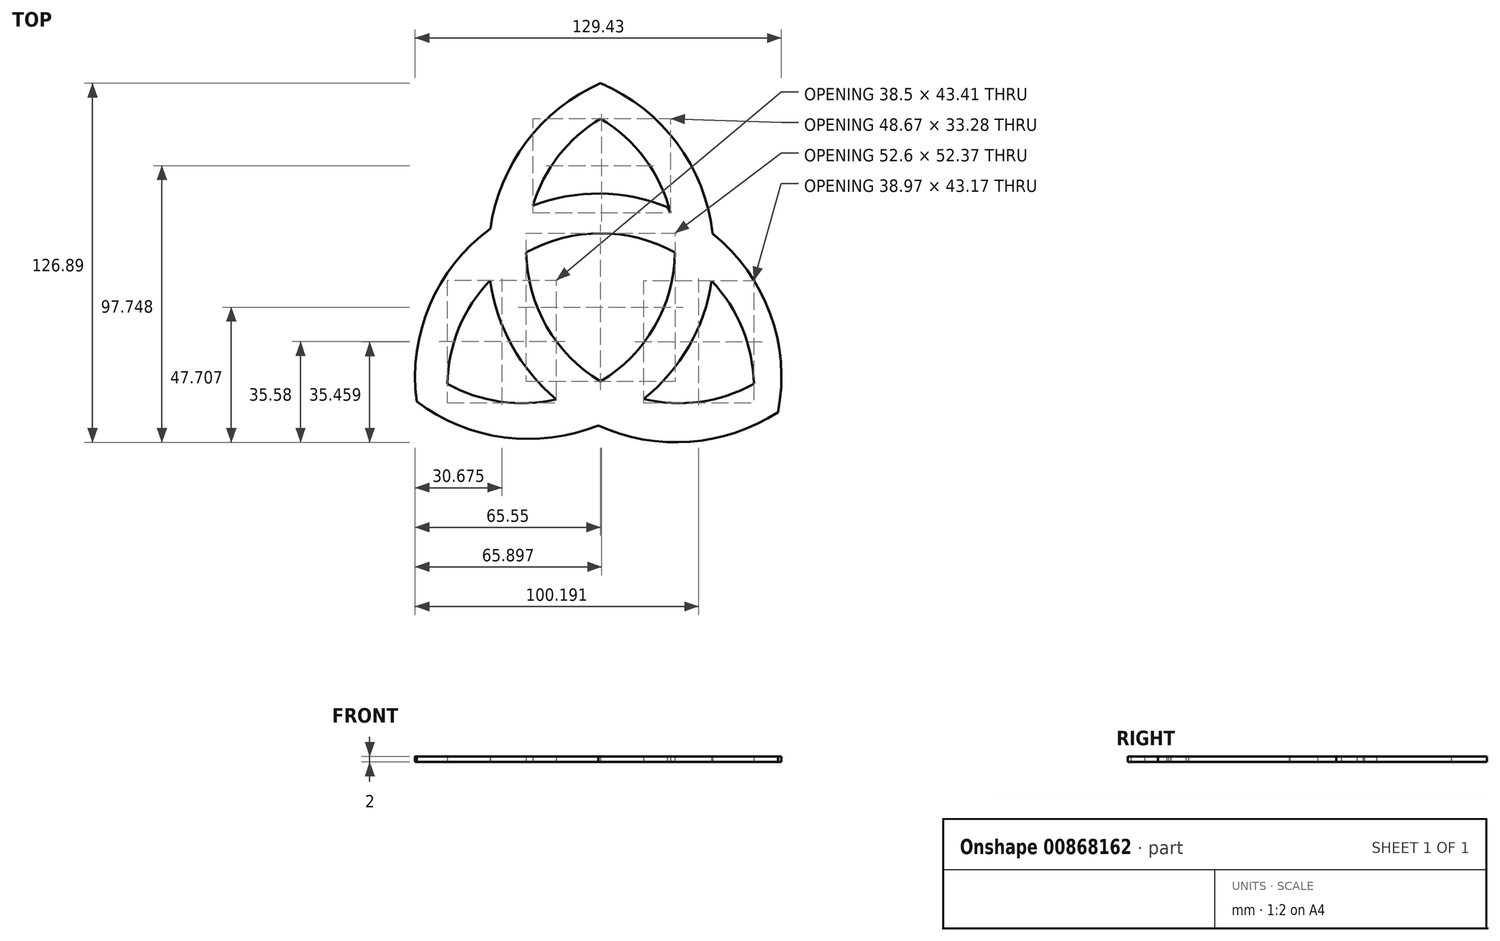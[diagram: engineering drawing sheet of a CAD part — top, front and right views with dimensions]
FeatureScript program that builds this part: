
annotation { "Feature Type Name" : "Feature", "Feature Type Description" : "" }
export const myFeature = defineFeature(function(context is Context, id is Id, definition is map)
    precondition{}
    {
        {
            var Q0;
            Q0=qCreatedBy(makeId("Top.planeOp"),FACE);
            var sketch = newSketch(context, id + "F0", { "sketchPlane" : qUnion([Q0])});
            skCircle(sketch, "E0", {"center": v(0, 0) * mm, "radius": 75 * mm});
            skCircle(sketch, "E1.cCircle", {"center": v(0, 0) * mm, "radius": 75 * mm, "construction": true});
            skLineSegment(sketch, "E1.0", {"start": v(23.6, 31.22) * mm, "end": v(24.68, 29.22) * mm});
            skLineSegment(sketch, "E2.0", {"start": v(25.24, 15.75) * mm, "end": v(26.26, 13.87) * mm});
            skArc(sketch, "E3", {"start": v(62.66, -41.22) * mm, "mid": v(59.93, -6.45) * mm, "end": v(39.56, 21.86) * mm});
            skArc(sketch, "E4", {"start": v(0, 75) * mm, "mid": v(-26.17, 54.36) * mm, "end": v(-38.97, 23.58) * mm});
            skArc(sketch, "E5", {"start": v(-64.95, -37.5) * mm, "mid": v(-34.02, -50.17) * mm, "end": v(-0.87, -45.91) * mm});
            skArc(sketch, "E6", {"start": v(54.13, -31.25) * mm, "mid": v(50.1, -11.65) * mm, "end": v(39.24, 5.16) * mm});
            skArc(sketch, "E7", {"start": v(0, 62.5) * mm, "mid": v(-14.86, 49.35) * mm, "end": v(-24, 31.73) * mm});
            skArc(sketch, "E8", {"start": v(-54.13, -31.25) * mm, "mid": v(-35.38, -37.54) * mm, "end": v(-15.62, -36.67) * mm});
            skArc(sketch, "E9.trimOffspring", {"start": v(-26.3, 15.18) * mm, "mid": v(0.76, -30.81) * mm, "end": v(54.13, -31.25) * mm});
            skArc(sketch, "E10.trimOffspring", {"start": v(-39.01, 5.4) * mm, "mid": v(-1, -45.86) * mm, "end": v(62.66, -41.22) * mm});
            skArc(sketch, "E11.trimOffspring", {"start": v(24.21, 30.97) * mm, "mid": v(-40.25, 22.63) * mm, "end": v(-64.95, -37.5) * mm});
            skArc(sketch, "E12.trimOffspring", {"start": v(26.3, 15.18) * mm, "mid": v(-27.07, 14.75) * mm, "end": v(-54.13, -31.25) * mm});
            skArc(sketch, "E13.trimOffspring", {"start": v(0, -30.37) * mm, "mid": v(26.3, 16.07) * mm, "end": v(0, 62.5) * mm});
            skArc(sketch, "E14.trimOffspring", {"start": v(15.16, -36.56) * mm, "mid": v(39.35, 23.53) * mm, "end": v(0, 75) * mm});
            skSolve(sketch);
        }
        {
            var Q0;
            {var subQ9=sQuery(id+"F0.wireOp",EDGE,"E1.0");Q0=makeQuery(id+"F0.imprint","IMPRINT",FACE,{"disambiguationData":[TD([[makeQuery(id+"F0.imprint","IMPRINT",EDGE,{"derivedFrom":subQ9}),-1.0]])]});}
            var Q1;
            {var subQ4=sQuery(id+"F0.wireOp",EDGE,"E4");Q1=makeQuery(id+"F0.imprint","IMPRINT",FACE,{"disambiguationData":[TD([[makeQuery(id+"F0.imprint","IMPRINT",EDGE,{"derivedFrom":subQ4}),1.0]])]});}
            var Q2;
            {var subQ9=sQuery(id+"F0.wireOp",EDGE,"E3");Q2=makeQuery(id+"F0.imprint","IMPRINT",FACE,{"disambiguationData":[TD([[makeQuery(id+"F0.imprint","IMPRINT",EDGE,{"derivedFrom":subQ9}),1.0]])]});}
            extrude(context, id + "F1", {"entities" : qUnion([Q0, Q1, Q2]), "depth" : 2 * mm, "offsetDistance" : 25 * mm});
        }
    });
